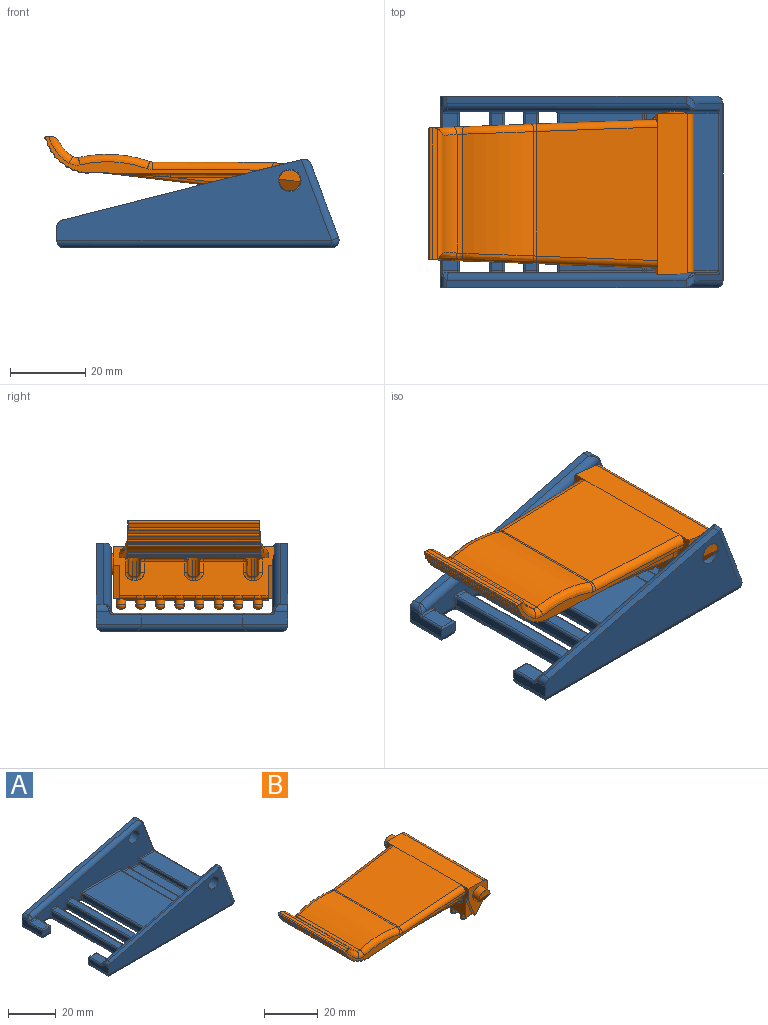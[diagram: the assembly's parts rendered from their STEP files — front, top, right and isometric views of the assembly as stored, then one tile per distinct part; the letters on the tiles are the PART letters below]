
ASSEMBLY  parts=2 mates=1
PART A: 159 faces, bbox 76.4x51.6x24.8 mm
  f0: plane 8x3.5mm, normal (0,0,-1), area 9.3mm2, adj f121,f123,f128,f131,f132
  f1: plane 5x2.5mm, normal (0,0,-1), area 2.7mm2, adj f127,f129,f132
  f2: plane 5x2.5mm, normal (0,0,-1), area 2.7mm2, adj f125,f126,f132
  f3: plane 47x42.61mm, normal (0,0,-1), area 1888mm2, adj f124,f132,f133,f138,f146,f148
  f4: plane 5x2.5mm, normal (0,0,-1), area 2.7mm2, adj f139,f140,f146
  f5: plane 5x2.5mm, normal (0,0,-1), area 2.7mm2, adj f141,f142,f146
  f6: plane 42x8.28mm, normal (0,0,1), area 347.7mm2, adj f39,f42,f43,f44
  f7: plane 7x4mm, normal (0,0,1), area 28mm2, adj f84,f86,f87,f88
  f8: plane 42x3mm, normal (0,0,1), area 126mm2, adj f94,f95,f99,f100
  f9: plane 42x22.16mm, normal (0,0,1), area 930.5mm2, adj f63,f64,f72,f73
  f10: plane 42x3mm, normal (0,0,1), area 126mm2, adj f106,f107,f111,f112
  f11: plane 12x3.44mm, normal (-1,0,0), area 33.5mm2, adj f16,f30,f82,f83,f115,f116,f131
  f12: plane 8x3.5mm, normal (0,0,-1), area 9.3mm2, adj f136,f143,f144,f146,f147
  f13: plane 73.11x21.51mm, normal (0,-1,0), area 920mm2, adj f18,f21,f32,f146,f150,f158
  f14: plane 71.18x19.99mm, normal (0,1,0), area 633.1mm2, adj f32,f37,f42,f45,f47,f52,f55,f58
  f15: plane 71.18x19.99mm, normal (0,-1,0), area 633.1mm2, adj f31,f38,f43,f46,f48,f53,f65,f66
  f16: plane 73.11x21.51mm, normal (0,1,0), area 920mm2, adj f11,f20,f31,f115,f132,f137
  f17: plane 7x4mm, normal (0,0,1), area 28mm2, adj f78,f80,f81,f82
  f18: plane 12x3.44mm, normal (-1,0,0), area 33.5mm2, adj f13,f26,f84,f85,f147,f155,f158
  f19: plane 47.56x20.18mm, normal (0.94,0,0.35), area 156.1mm2, adj f37,f38,f39,f40,f41,f119,f130,f137
  f20: plane 63.76x16.18mm, normal (-0.25,0,0.97), area 131.6mm2, adj f16,f115,f118,f120,f130,f137
  f21: plane 63.76x16.18mm, normal (-0.25,0,0.97), area 131.6mm2, adj f13,f150,f151,f154,f156,f158
  f22: plane 42x2.5mm, normal (1,0,0), area 105mm2, adj f96,f100,f102,f135
  f23: plane 42x2.5mm, normal (-1,0,0), area 105mm2, adj f103,f105,f106,f134
  f24: plane 42x2.5mm, normal (1,0,0), area 105mm2, adj f108,f112,f114,f134
  f25: plane 42x2.5mm, normal (-1,0,0), area 105mm2, adj f55,f64,f65,f133
  f26: plane 5x2.5mm, normal (0,1,0), area 12.5mm2, adj f18,f28,f86,f144
  f27: plane 42x2.5mm, normal (-1,0,0), area 105mm2, adj f91,f93,f94,f135
  f28: plane 7.5x2.5mm, normal (1,0,0), area 18.8mm2, adj f26,f88,f90,f136
  f29: plane 7.5x2.5mm, normal (1,0,0), area 18.8mm2, adj f30,f77,f78,f121
  f30: plane 5x2.5mm, normal (0,-1,0), area 12.5mm2, adj f11,f29,f80,f123
  f31: cylinder r=3mm len=6mm, axis (0,-1,0), area 75.4mm2, adj f15,f16,f120
  f32: cylinder r=3mm len=6mm, axis (0,-1,0), area 75.4mm2, adj f13,f14,f154
  f33: plane 42x1.5mm, normal (-1,0,0), area 63mm2, adj f44,f47,f48,f49
  f34: plane 42x4.5mm, normal (0,0,1), area 189mm2, adj f49,f52,f53,f57
  f35: plane 42x0.5mm, normal (1,0,0), area 21mm2, adj f62,f71,f72,f76
  f36: plane 42x4.34mm, normal (0,0,1), area 182.5mm2, adj f60,f61,f70,f71
  f37: cylinder r=0.5mm len=16.67mm, axis (0.35,0,-0.94), area 13.8mm2, adj f14,f19,f40,f152
  f38: cylinder r=0.5mm len=16.67mm, axis (-0.35,0,0.94), area 13.8mm2, adj f15,f19,f41,f119
  f39: cylinder r=0.5mm len=42mm, axis (0,1,0), area 25.5mm2, adj f6,f19,f40,f41
  f40: bspline ~1.17x1.17mm, area 0.8mm2, adj f19,f37,f39,f42
  f41: bspline ~1.05x1.03mm, area 0.8mm2, adj f19,f38,f39,f43
  f42: cylinder r=0.5mm len=8.28mm, axis (-1,0,0), area 6.4mm2, adj f6,f14,f40,f45
  f43: cylinder r=0.5mm len=8.28mm, axis (1,0,0), area 6.4mm2, adj f6,f15,f41,f46
  f44: cylinder r=0.5mm len=42mm, axis (0,-1,0), area 33mm2, adj f6,f33,f45,f46
  f45: torus R=1mm, axis (0,-1,0), area 0.8mm2, adj f14,f42,f44,f47
  f46: torus R=1mm, axis (0,-1,0), area 0.8mm2, adj f15,f43,f44,f48
  f47: cylinder r=0.5mm len=1.5mm, axis (0,0,1), area 1.2mm2, adj f14,f33,f45,f50
  f48: cylinder r=0.5mm len=1.5mm, axis (0,0,-1), area 1.2mm2, adj f15,f33,f46,f51
  f49: cylinder r=0.5mm len=42mm, axis (0,1,0), area 33mm2, adj f33,f34,f50,f51
  f50: sphere r=0.5mm, area 0.4mm2, adj f47,f49,f52
  f51: sphere r=0.5mm, area 0.2mm2, adj f48,f49,f53
  f52: cylinder r=0.5mm len=4.5mm, axis (-1,0,0), area 3.5mm2, adj f14,f34,f50,f54
  f53: cylinder r=0.5mm len=4.5mm, axis (1,0,0), area 3.5mm2, adj f15,f34,f51,f56
  f54: sphere r=0.5mm, area 0.4mm2, adj f52,f57,f58
  f55: cylinder r=0.5mm len=2.5mm, axis (0,0,1), area 2mm2, adj f14,f25,f59,f138
  f56: sphere r=0.5mm, area 0.5mm2, adj f53,f57,f66
  f57: cylinder r=0.5mm len=42mm, axis (0,-1,0), area 33mm2, adj f34,f54,f56,f60
  f58: torus R=1mm, axis (0,-1,0), area 0.8mm2, adj f14,f54,f60,f61
  f59: torus R=1mm, axis (0,-1,0), area 0.8mm2, adj f14,f55,f63,f64
  f60: cylinder r=0.5mm len=42mm, axis (0,1,0), area 33mm2, adj f36,f57,f58,f66
  f61: cylinder r=0.5mm len=4.34mm, axis (-1,0,0), area 3.4mm2, adj f14,f36,f58,f67
  f62: cylinder r=0.5mm len=0.5mm, axis (0,0,-1), area 0.4mm2, adj f14,f35,f67,f68
  f63: cylinder r=0.5mm len=22.16mm, axis (-1,0,0), area 17.4mm2, adj f9,f14,f59,f68
  f64: cylinder r=0.5mm len=42mm, axis (0,-1,0), area 33mm2, adj f9,f25,f59,f69
  f65: cylinder r=0.5mm len=2.5mm, axis (0,0,-1), area 2mm2, adj f15,f25,f69,f124
  f66: torus R=1mm, axis (0,-1,0), area 0.8mm2, adj f15,f56,f60,f70
  f67: sphere r=0.5mm, area 0.4mm2, adj f61,f62,f71
  f68: torus R=1mm, axis (0,-1,0), area 0.8mm2, adj f14,f62,f63,f72
  f69: torus R=1mm, axis (0,-1,0), area 0.8mm2, adj f15,f64,f65,f73
  f70: cylinder r=0.5mm len=4.34mm, axis (1,0,0), area 3.4mm2, adj f15,f36,f66,f74
  f71: cylinder r=0.5mm len=42mm, axis (0,-1,0), area 33mm2, adj f35,f36,f67,f74
  f72: cylinder r=0.5mm len=42mm, axis (0,1,0), area 33mm2, adj f9,f35,f68,f75
  f73: cylinder r=0.5mm len=22.16mm, axis (1,0,0), area 17.4mm2, adj f9,f15,f69,f75
  f74: sphere r=0.5mm, area 0.5mm2, adj f70,f71,f76
  f75: torus R=1mm, axis (0,-1,0), area 0.8mm2, adj f15,f72,f73,f76
  f76: cylinder r=0.5mm len=0.5mm, axis (0,0,1), area 0.4mm2, adj f15,f35,f74,f75
  f77: cylinder r=0.5mm len=2.5mm, axis (0,0,1), area 2mm2, adj f15,f29,f79,f128
  f78: cylinder r=0.5mm len=7.5mm, axis (0,1,0), area 5.7mm2, adj f17,f29,f79,f80
  f79: torus R=1mm, axis (0,-1,0), area 0.8mm2, adj f15,f77,f78,f81
  f80: cylinder r=0.5mm len=5mm, axis (1,0,0), area 3.5mm2, adj f17,f30,f78,f82
  f81: cylinder r=0.5mm len=4mm, axis (1,0,0), area 3.1mm2, adj f15,f17,f79,f83,f118
  f82: cylinder r=0.5mm len=7.5mm, axis (0,1,0), area 5.7mm2, adj f11,f17,f80,f83
  f83: torus R=1mm, axis (-1,0,0), area 0.7mm2, adj f11,f81,f82,f116
  f84: cylinder r=0.5mm len=7.5mm, axis (0,1,0), area 5.7mm2, adj f7,f18,f85,f86
  f85: torus R=1mm, axis (-1,0,0), area 0.7mm2, adj f18,f84,f87,f155
  f86: cylinder r=0.5mm len=5mm, axis (-1,0,0), area 3.5mm2, adj f7,f26,f84,f88
  f87: cylinder r=0.5mm len=4mm, axis (-1,0,0), area 3.1mm2, adj f7,f14,f85,f89,f156
  f88: cylinder r=0.5mm len=7.5mm, axis (0,1,0), area 5.7mm2, adj f7,f28,f86,f89
  f89: torus R=1mm, axis (0,-1,0), area 0.8mm2, adj f14,f87,f88,f90
  f90: cylinder r=0.5mm len=2.5mm, axis (0,0,-1), area 2mm2, adj f14,f28,f89,f143
  f91: cylinder r=0.5mm len=2.5mm, axis (0,0,-1), area 2mm2, adj f15,f27,f92,f129
  f92: torus R=1mm, axis (0,-1,0), area 0.8mm2, adj f15,f91,f94,f95
  f93: cylinder r=0.5mm len=2.5mm, axis (0,0,1), area 2mm2, adj f14,f27,f97,f142
  f94: cylinder r=0.5mm len=42mm, axis (0,-1,0), area 33mm2, adj f8,f27,f92,f97
  f95: cylinder r=0.5mm len=3mm, axis (1,0,0), area 2.4mm2, adj f8,f15,f92,f98
  f96: cylinder r=0.5mm len=2.5mm, axis (0,0,1), area 2mm2, adj f15,f22,f98,f127
  f97: torus R=1mm, axis (0,-1,0), area 0.8mm2, adj f14,f93,f94,f99
  f98: torus R=1mm, axis (0,-1,0), area 0.8mm2, adj f15,f95,f96,f100
  f99: cylinder r=0.5mm len=3mm, axis (-1,0,0), area 2.4mm2, adj f8,f14,f97,f101
  f100: cylinder r=0.5mm len=42mm, axis (0,1,0), area 33mm2, adj f8,f22,f98,f101
  f101: torus R=1mm, axis (0,-1,0), area 0.8mm2, adj f14,f99,f100,f102
  f102: cylinder r=0.5mm len=2.5mm, axis (0,0,-1), area 2mm2, adj f14,f22,f101,f141
  f103: cylinder r=0.5mm len=2.5mm, axis (0,0,-1), area 2mm2, adj f15,f23,f104,f126
  f104: torus R=1mm, axis (0,-1,0), area 0.8mm2, adj f15,f103,f106,f107
  f105: cylinder r=0.5mm len=2.5mm, axis (0,0,1), area 2mm2, adj f14,f23,f109,f140
  f106: cylinder r=0.5mm len=42mm, axis (0,-1,0), area 33mm2, adj f10,f23,f104,f109
  f107: cylinder r=0.5mm len=3mm, axis (1,0,0), area 2.4mm2, adj f10,f15,f104,f110
  f108: cylinder r=0.5mm len=2.5mm, axis (0,0,1), area 2mm2, adj f15,f24,f110,f125
  f109: torus R=1mm, axis (0,-1,0), area 0.8mm2, adj f14,f105,f106,f111
  f110: torus R=1mm, axis (0,-1,0), area 0.8mm2, adj f15,f107,f108,f112
  f111: cylinder r=0.5mm len=3mm, axis (-1,0,0), area 2.4mm2, adj f10,f14,f109,f113
  f112: cylinder r=0.5mm len=42mm, axis (0,1,0), area 33mm2, adj f10,f24,f110,f113
  f113: torus R=1mm, axis (0,-1,0), area 0.8mm2, adj f14,f111,f112,f114
  f114: cylinder r=0.5mm len=2.5mm, axis (0,0,-1), area 2mm2, adj f14,f24,f113,f139
  f115: cylinder r=2mm len=3.49mm, axis (0,-1,0), area 7.3mm2, adj f11,f16,f20,f117
  f116: bspline ~0.92x0.65mm, area 0.1mm2, adj f11,f83,f117,f118
  f117: bspline ~2.26x2.05mm, area 0.9mm2, adj f115,f116,f118
  f118: bspline ~2.21x2.03mm, area 3.4mm2, adj f20,f81,f116,f117,f120
  f119: bspline ~0.54x0.51mm, area 0.2mm2, adj f19,f38,f120,f122
  f120: cylinder r=2mm len=65.49mm, axis (-0.97,0,-0.25), area 208.3mm2, adj f15,f20,f31,f118,f119,f122
  f121: cylinder r=2mm len=7.5mm, axis (0,1,0), area 20.4mm2, adj f0,f29,f123,f128
  f122: bspline ~2.4x2mm, area 1mm2, adj f119,f120,f130
  f123: cylinder r=2mm len=5mm, axis (1,0,0), area 9.4mm2, adj f0,f30,f121,f131
  f124: torus R=2.5mm, axis (0,0,1), area 6.1mm2, adj f3,f65,f132,f133
  f125: torus R=2.5mm, axis (0,0,1), area 6.1mm2, adj f2,f108,f132,f134
  f126: torus R=2.5mm, axis (0,0,1), area 6.1mm2, adj f2,f103,f132,f134
  f127: torus R=2.5mm, axis (0,0,1), area 6.1mm2, adj f1,f96,f132,f135
  f128: torus R=2.5mm, axis (0,0,1), area 6.1mm2, adj f0,f77,f121,f132
  f129: torus R=2.5mm, axis (0,0,1), area 6.1mm2, adj f1,f91,f132,f135
  f130: cylinder r=2mm len=3.48mm, axis (0,1,0), area 5.1mm2, adj f19,f20,f122,f137
  f131: cylinder r=2mm len=12mm, axis (0,-1,0), area 31.4mm2, adj f0,f11,f123,f132
  f132: cylinder r=2mm len=73.11mm, axis (-1,0,0), area 273.7mm2, adj f0,f1,f2,f3,f15,f16,f124,f125
  f133: cylinder r=2mm len=42mm, axis (0,-1,0), area 131.9mm2, adj f3,f25,f124,f138
  f134: cylinder r=2mm len=42mm, axis (0,1,0), area 263.9mm2, adj f23,f24,f125,f126,f139,f140
  f135: cylinder r=2mm len=42mm, axis (0,1,0), area 263.9mm2, adj f22,f27,f127,f129,f141,f142
  f136: cylinder r=2mm len=7.5mm, axis (0,1,0), area 20.4mm2, adj f12,f28,f143,f144
  f137: cylinder r=2mm len=22.21mm, axis (-0.35,0,0.94), area 69.8mm2, adj f16,f19,f20,f130,f145
  f138: torus R=2.5mm, axis (0,0,1), area 6.1mm2, adj f3,f55,f133,f146
  f139: torus R=2.5mm, axis (0,0,1), area 6.1mm2, adj f4,f114,f134,f146
  f140: torus R=2.5mm, axis (0,0,1), area 6.1mm2, adj f4,f105,f134,f146
  f141: torus R=2.5mm, axis (0,0,1), area 6.1mm2, adj f5,f102,f135,f146
  f142: torus R=2.5mm, axis (0,0,1), area 6.1mm2, adj f5,f93,f135,f146
  f143: torus R=2.5mm, axis (0,0,1), area 6.1mm2, adj f12,f90,f136,f146
  f144: cylinder r=2mm len=5mm, axis (-1,0,0), area 9.4mm2, adj f12,f26,f136,f147
  f145: sphere r=2mm, area 5.1mm2, adj f132,f137,f148
  f146: cylinder r=2mm len=73.11mm, axis (1,0,0), area 273.7mm2, adj f3,f4,f5,f12,f13,f14,f138,f139
  f147: cylinder r=2mm len=12mm, axis (0,-1,0), area 31.4mm2, adj f12,f18,f144,f146
  f148: cylinder r=2mm len=47mm, axis (0,1,0), area 181.4mm2, adj f3,f19,f145,f149
  f149: sphere r=2mm, area 7.7mm2, adj f146,f148,f150
  f150: cylinder r=2mm len=22.21mm, axis (-0.35,0,0.94), area 69.8mm2, adj f13,f19,f21,f149,f151
  f151: cylinder r=2mm len=3.48mm, axis (0,1,0), area 5.1mm2, adj f19,f21,f150,f153
  f152: bspline ~0.54x0.51mm, area 0.2mm2, adj f19,f37,f153,f154
  f153: bspline ~2.4x2mm, area 1mm2, adj f151,f152,f154
  f154: cylinder r=2mm len=65.49mm, axis (0.97,0,0.25), area 208.3mm2, adj f14,f21,f32,f152,f153,f156
  f155: bspline ~0.92x0.65mm, area 0.1mm2, adj f18,f85,f156,f157
  f156: bspline ~5.37x2.68mm, area 3.4mm2, adj f21,f87,f154,f155,f157
  f157: bspline ~2.26x2.05mm, area 0.9mm2, adj f155,f156,f158
  f158: cylinder r=2mm len=3.49mm, axis (0,-1,0), area 7.3mm2, adj f13,f18,f21,f157
PART B: 151 faces, bbox 74.5x53.5x20.7 mm
  f0: plane 13.5x10mm, normal (0,1,0), area 69.4mm2, adj f17,f19,f20,f22,f23,f73,f76,f77
  f1: plane 39.5x0.5mm, normal (0.93,0,0.36), area 21.2mm2, adj f14,f23,f24,f78
  f2: cylinder r=2.8mm len=5.6mm, axis (0,1,0), area 61.6mm2, adj f3,f18,f72
  f3: plane 5.6x2.78mm, normal (0,-1,0), area 12.2mm2, adj f2,f72
  f4: plane 49.04x39.5mm, normal (0.11,0,-0.99), area 1208.5mm2, adj f15,f16,f20,f61,f94,f97,f99,f102
  f5: cylinder r=12.71mm len=35.85mm, axis (0,-1,0), area 35.7mm2, adj f15,f16,f53,f62
  f6: cylinder r=12.71mm len=35mm, axis (0,-1,0), area 3mm2, adj f15,f16,f60,f93
  f7: cylinder r=12.71mm len=35.06mm, axis (0,-1,0), area 35mm2, adj f15,f16,f59,f60
  f8: cylinder r=12.71mm len=35.14mm, axis (0,-1,0), area 35mm2, adj f15,f16,f58,f59
  f9: cylinder r=12.71mm len=35.23mm, axis (0,-1,0), area 35.1mm2, adj f15,f16,f57,f58
  f10: cylinder r=12.71mm len=35.33mm, axis (0,-1,0), area 35.2mm2, adj f15,f16,f56,f57
  f11: cylinder r=12.71mm len=35.45mm, axis (0,-1,0), area 35.3mm2, adj f15,f16,f55,f56
  f12: cylinder r=12.71mm len=35.58mm, axis (0,-1,0), area 35.5mm2, adj f15,f16,f54,f55
  f13: cylinder r=12.71mm len=35.71mm, axis (0,-1,0), area 35.6mm2, adj f15,f16,f53,f54
  f14: plane 39.5x2.5mm, normal (0,0,-1), area 66.5mm2, adj f1,f24,f29,f31,f33,f35,f37,f39
  f15: plane 61.11x8.78mm, normal (-0.04,-1,0), area 92.8mm2, adj f4,f5,f6,f7,f8,f9,f10,f11
  f16: plane 61.11x8.78mm, normal (-0.04,1,0), area 92.8mm2, adj f4,f5,f6,f7,f8,f9,f10,f11
  f17: plane 43x8mm, normal (0,0,1), area 344mm2, adj f0,f18,f20,f26,f76
  f18: plane 13.5x10mm, normal (0,-1,0), area 69.4mm2, adj f2,f17,f19,f20,f22,f23,f25,f76
  f19: plane 43x3mm, normal (1,0,0), area 129mm2, adj f0,f18,f22,f76
  f20: plane 43.12x13.26mm, normal (-1,0,0), area 306.3mm2, adj f0,f4,f15,f16,f17,f18,f24,f25
  f21: plane 35.12x1.39mm, normal (0,0,1), area 47.3mm2, adj f15,f16,f80,f81,f83,f93
  f22: plane 43x8.5mm, normal (0.81,0,-0.59), area 450.9mm2, adj f0,f18,f19,f23
  f23: plane 43x0.56mm, normal (0,0,-1), area 23.9mm2, adj f0,f1,f18,f22,f25,f77
  f24: plane 9x3.5mm, normal (0,-1,0), area 15.5mm2, adj f1,f14,f20,f25,f136
  f25: plane 8.5x3.31mm, normal (-0.93,0,-0.36), area 16mm2, adj f18,f20,f23,f24
  f26: plane 35.51x31.94mm, normal (-0.11,0,0.99), area 1103.7mm2, adj f17,f86,f90,f92
  f27: cylinder r=34.04mm len=33.06mm, axis (0,-1,0), area 624.1mm2, adj f84,f85,f89,f90
  f28: cylinder r=9.71mm len=31.52mm, axis (0,-1,0), area 177.3mm2, adj f80,f81,f83,f84
  f29: cylinder r=1.25mm len=2.5mm, axis (0,0,1), area 11.8mm2, adj f14,f52,f137
  f30: plane 0.5x0.5mm, normal (0,0,-1), area 0.2mm2, adj f52
  f31: cylinder r=1.25mm len=2.5mm, axis (0,0,1), area 11.8mm2, adj f14,f51,f139
  f32: plane 0.5x0.5mm, normal (0,0,-1), area 0.2mm2, adj f51
  f33: cylinder r=1.25mm len=2.5mm, axis (0,0,1), area 11.8mm2, adj f14,f50,f141
  f34: plane 0.5x0.5mm, normal (0,0,-1), area 0.2mm2, adj f50
  f35: cylinder r=1.25mm len=2.5mm, axis (0,0,1), area 11.8mm2, adj f14,f49,f143
  f36: plane 0.5x0.5mm, normal (0,0,-1), area 0.2mm2, adj f49
  f37: cylinder r=1.25mm len=2.5mm, axis (0,0,1), area 11.8mm2, adj f14,f48,f145
  f38: plane 0.5x0.5mm, normal (0,0,-1), area 0.2mm2, adj f48
  f39: cylinder r=1.25mm len=2.5mm, axis (0,0,1), area 11.8mm2, adj f14,f47,f147
  f40: plane 0.5x0.5mm, normal (0,0,-1), area 0.2mm2, adj f47
  f41: cylinder r=1.25mm len=2.5mm, axis (0,0,1), area 11.8mm2, adj f14,f46,f149
  f42: plane 0.5x0.5mm, normal (0,0,-1), area 0.2mm2, adj f46
  f43: cylinder r=1.25mm len=2.5mm, axis (0,0,1), area 11.9mm2, adj f14,f45,f78,f79,f150
  f44: plane 0.5x0.5mm, normal (0,0,-1), area 0.2mm2, adj f45
  f45: torus R=0.25mm, axis (0,0,-1), area 8.8mm2, adj f43,f44
  f46: torus R=0.25mm, axis (0,0,-1), area 8.8mm2, adj f41,f42
  f47: torus R=0.25mm, axis (0,0,-1), area 8.8mm2, adj f39,f40
  f48: torus R=0.25mm, axis (0,0,-1), area 8.8mm2, adj f37,f38
  f49: torus R=0.25mm, axis (0,0,-1), area 8.8mm2, adj f35,f36
  f50: torus R=0.25mm, axis (0,0,-1), area 8.8mm2, adj f33,f34
  f51: torus R=0.25mm, axis (0,0,-1), area 8.8mm2, adj f31,f32
  f52: torus R=0.25mm, axis (0,0,-1), area 8.8mm2, adj f29,f30
  f53: cylinder r=0.5mm len=35.78mm, axis (0,-1,0), area 38.8mm2, adj f5,f13,f15,f16
  f54: cylinder r=0.5mm len=35.64mm, axis (0,-1,0), area 38.7mm2, adj f12,f13,f15,f16
  f55: cylinder r=0.5mm len=35.51mm, axis (0,-1,0), area 38.6mm2, adj f11,f12,f15,f16
  f56: cylinder r=0.5mm len=35.39mm, axis (0,-1,0), area 38.4mm2, adj f10,f11,f15,f16
  f57: cylinder r=0.5mm len=35.28mm, axis (0,-1,0), area 38.3mm2, adj f9,f10,f15,f16
  f58: cylinder r=0.5mm len=35.18mm, axis (0,-1,0), area 38.2mm2, adj f8,f9,f15,f16
  f59: cylinder r=0.5mm len=35.09mm, axis (0,-1,0), area 38.1mm2, adj f7,f8,f15,f16
  f60: cylinder r=0.5mm len=35.03mm, axis (0,-1,0), area 38mm2, adj f6,f7,f15,f16
  f61: cylinder r=12.71mm len=35.92mm, axis (0,-1,0), area 17mm2, adj f4,f15,f16,f62
  f62: cylinder r=0.5mm len=35.92mm, axis (0,-1,0), area 39mm2, adj f5,f15,f16,f61
  f63: plane 25.69x2.88mm, normal (0,-1,0), area 37mm2, adj f94,f95,f96
  f64: plane 25.69x2.88mm, normal (0,1,0), area 37mm2, adj f100,f104,f105
  f65: plane 43.52x1mm, normal (0,0,-1), area 43.5mm2, adj f95,f99,f100,f101
  f66: plane 25.69x2.88mm, normal (0,1,0), area 37mm2, adj f115,f123,f124
  f67: plane 43.52x1mm, normal (0,0,-1), area 43.5mm2, adj f110,f114,f115,f116
  f68: plane 25.69x2.88mm, normal (0,-1,0), area 37mm2, adj f109,f110,f111
  f69: plane 25.69x2.88mm, normal (0,1,0), area 37mm2, adj f117,f121,f122
  f70: plane 43.52x1mm, normal (0,0,-1), area 43.5mm2, adj f121,f125,f129,f130
  f71: plane 25.69x2.88mm, normal (0,-1,0), area 37mm2, adj f129,f132,f135
  f72: plane 9.06x6.28mm, normal (0,-0.85,-0.52), area 14.6mm2, adj f2,f3
  f73: cylinder r=2.8mm len=5.6mm, axis (0,-1,0), area 61.6mm2, adj f0,f74,f75
  f74: plane 5.6x2.8mm, normal (0,1,0), area 12.3mm2, adj f73,f75
  f75: plane 9.04x6.24mm, normal (0,0.85,-0.52), area 14.5mm2, adj f73,f74
  f76: cylinder r=2mm len=43mm, axis (0,-1,0), area 135.1mm2, adj f0,f17,f18,f19
  f77: plane 8.5x3.31mm, normal (-0.93,0,-0.36), area 16mm2, adj f0,f20,f23,f78
  f78: plane 9x3.5mm, normal (0,1,0), area 15.6mm2, adj f1,f14,f20,f43,f77,f79,f150
  f79: plane 2.39x0.89mm, normal (0,0,1), area 1.6mm2, adj f43,f78
  f80: bspline ~7.16x6.96mm, area 23.2mm2, adj f16,f21,f28,f81,f82
  f81: cylinder r=2mm len=34.63mm, axis (0,-1,0), area 66.5mm2, adj f21,f28,f80,f83
  f82: bspline ~3.01x2.18mm, area 6.6mm2, adj f16,f80,f84,f85
  f83: bspline ~7.16x6.96mm, area 23.2mm2, adj f15,f21,f28,f81,f87
  f84: cylinder r=2mm len=31.74mm, axis (0,-1,0), area 48.8mm2, adj f27,f28,f82,f87
  f85: bspline ~18.97x3.87mm, area 59.2mm2, adj f16,f27,f82,f88
  f86: cylinder r=2mm len=32.11mm, axis (0.99,0.04,0.11), area 100.6mm2, adj f16,f20,f26,f88
  f87: bspline ~3.01x2.18mm, area 6.6mm2, adj f15,f83,f84,f89
  f88: bspline ~2.05x2.05mm, area 2.9mm2, adj f16,f85,f86,f90
  f89: bspline ~18.97x3.87mm, area 59.2mm2, adj f15,f27,f87,f91
  f90: cylinder r=2mm len=33.16mm, axis (0,-1,0), area 22.2mm2, adj f26,f27,f88,f91
  f91: bspline ~2.05x2.05mm, area 2.9mm2, adj f15,f89,f90,f92
  f92: cylinder r=2mm len=32.11mm, axis (-0.99,0.04,-0.11), area 100.6mm2, adj f15,f20,f26,f91
  f93: cylinder r=2mm len=35.05mm, axis (0,-1,0), area 24mm2, adj f6,f15,f16,f21
  f94: cylinder r=1mm len=26.91mm, axis (-0.99,0,-0.11), area 41.5mm2, adj f4,f63,f96,f97
  f95: cylinder r=1mm len=43.52mm, axis (1,0,0), area 58.2mm2, adj f63,f65,f97,f98
  f96: cylinder r=1mm len=4mm, axis (0,0,-1), area 5.4mm2, adj f20,f63,f94,f98
  f97: bspline ~17.94x2mm, area 18mm2, adj f4,f94,f95,f99
  f98: torus R=2mm, axis (1,0,0), area 3.4mm2, adj f20,f95,f96,f101
  f99: cylinder r=1mm len=1mm, axis (0,1,0), area 0.1mm2, adj f4,f65,f97,f102
  f100: cylinder r=1mm len=43.52mm, axis (-1,0,0), area 58.2mm2, adj f64,f65,f102,f103
  f101: cylinder r=1mm len=1mm, axis (0,1,0), area 1.6mm2, adj f20,f65,f98,f103
  f102: bspline ~17.94x2mm, area 18mm2, adj f4,f99,f100,f104
  f103: torus R=2mm, axis (1,0,0), area 3.4mm2, adj f20,f100,f101,f105
  f104: cylinder r=1mm len=25.8mm, axis (0.99,0,0.11), area 40.6mm2, adj f4,f64,f102,f106
  f105: cylinder r=1mm len=2.88mm, axis (0,0,1), area 4.5mm2, adj f20,f64,f103,f106
  f106: sphere r=1mm, area 1.7mm2, adj f104,f105,f107
  f107: cylinder r=1mm len=10.75mm, axis (0,-1,0), area 18.1mm2, adj f4,f20,f106,f108
  f108: sphere r=1mm, area 1.7mm2, adj f107,f109,f111
  f109: cylinder r=1mm len=25.8mm, axis (-0.99,0,-0.11), area 40.6mm2, adj f4,f68,f108,f112
  f110: cylinder r=1mm len=43.52mm, axis (-1,0,0), area 58.2mm2, adj f67,f68,f112,f113
  f111: cylinder r=1mm len=2.88mm, axis (0,0,-1), area 4.5mm2, adj f20,f68,f108,f113
  f112: bspline ~17.94x2mm, area 18mm2, adj f4,f109,f110,f114
  f113: torus R=2mm, axis (1,0,0), area 3.4mm2, adj f20,f110,f111,f116
  f114: cylinder r=1mm len=1mm, axis (0,1,0), area 0.1mm2, adj f4,f67,f112,f118
  f115: cylinder r=1mm len=43.52mm, axis (1,0,0), area 58.2mm2, adj f66,f67,f118,f119
  f116: cylinder r=1mm len=1mm, axis (0,1,0), area 1.6mm2, adj f20,f67,f113,f119
  f117: cylinder r=1mm len=4mm, axis (0,0,1), area 5.4mm2, adj f20,f69,f120,f122
  f118: bspline ~17.94x2mm, area 18mm2, adj f4,f114,f115,f123
  f119: torus R=2mm, axis (1,0,0), area 3.4mm2, adj f20,f115,f116,f124
  f120: torus R=2mm, axis (1,0,0), area 3.4mm2, adj f20,f117,f121,f125
  f121: cylinder r=1mm len=43.52mm, axis (1,0,0), area 58.2mm2, adj f69,f70,f120,f126
  f122: cylinder r=1mm len=26.91mm, axis (0.99,0,0.11), area 41.5mm2, adj f4,f69,f117,f126
  f123: cylinder r=1mm len=25.8mm, axis (0.99,0,0.11), area 40.6mm2, adj f4,f66,f118,f127
  f124: cylinder r=1mm len=2.88mm, axis (0,0,1), area 4.5mm2, adj f20,f66,f119,f127
  f125: cylinder r=1mm len=1mm, axis (0,1,0), area 1.6mm2, adj f20,f70,f120,f128
  f126: bspline ~17.94x2mm, area 18mm2, adj f4,f121,f122,f130
  f127: sphere r=1mm, area 1.7mm2, adj f123,f124,f131
  f128: torus R=2mm, axis (1,0,0), area 3.4mm2, adj f20,f125,f129,f132
  f129: cylinder r=1mm len=43.52mm, axis (-1,0,0), area 58.2mm2, adj f70,f71,f128,f133
  f130: cylinder r=1mm len=1mm, axis (0,1,0), area 0.1mm2, adj f4,f70,f126,f133
  f131: cylinder r=1mm len=10.75mm, axis (0,-1,0), area 18.1mm2, adj f4,f20,f127,f134
  f132: cylinder r=1mm len=2.88mm, axis (0,0,-1), area 4.5mm2, adj f20,f71,f128,f134
  f133: bspline ~17.94x2mm, area 18mm2, adj f4,f129,f130,f135
  f134: sphere r=1mm, area 1.7mm2, adj f131,f132,f135
  f135: cylinder r=1mm len=25.8mm, axis (-0.99,0,-0.11), area 40.6mm2, adj f4,f71,f133,f134
  f136: cylinder r=1mm len=1.74mm, axis (0,-1,0), area 2.7mm2, adj f14,f20,f24,f137
  f137: bspline ~2x1mm, area 2.4mm2, adj f20,f29,f136,f138
  f138: cylinder r=1mm len=3.2mm, axis (0,-1,0), area 5mm2, adj f14,f20,f137,f139
  f139: bspline ~2x1mm, area 2.4mm2, adj f20,f31,f138,f140
  f140: cylinder r=1mm len=3.2mm, axis (0,-1,0), area 5mm2, adj f14,f20,f139,f141
  f141: bspline ~2x1mm, area 2.4mm2, adj f20,f33,f140,f142
  f142: cylinder r=1mm len=3.2mm, axis (0,-1,0), area 5mm2, adj f14,f20,f141,f143
  f143: bspline ~2x1mm, area 2.4mm2, adj f20,f35,f142,f144
  f144: cylinder r=1mm len=3.2mm, axis (0,-1,0), area 5mm2, adj f14,f20,f143,f145
  f145: bspline ~2x1mm, area 2.4mm2, adj f20,f37,f144,f146
  f146: cylinder r=1mm len=3.2mm, axis (0,-1,0), area 5mm2, adj f14,f20,f145,f147
  f147: bspline ~2x1mm, area 2.4mm2, adj f20,f39,f146,f148
  f148: cylinder r=1mm len=3.2mm, axis (0,-1,0), area 5mm2, adj f14,f20,f147,f149
  f149: bspline ~2x1mm, area 2.4mm2, adj f20,f41,f148,f150
  f150: cylinder r=1mm len=4.56mm, axis (0,-1,0), area 6.6mm2, adj f14,f20,f43,f78,f149
PLACE A rot(axis=(0.97,-0.24,0.01),0deg) t=(-115.77,-5.72,85.02)mm fixed
PLACE B rot(axis=(0,1,0),6.7deg) t=(-123.13,74.18,96.76)mm
MATE revolute B.f2 <-> A.f31  axis (0,-1,0) through (-91.77,-31.22,102.95)mm
